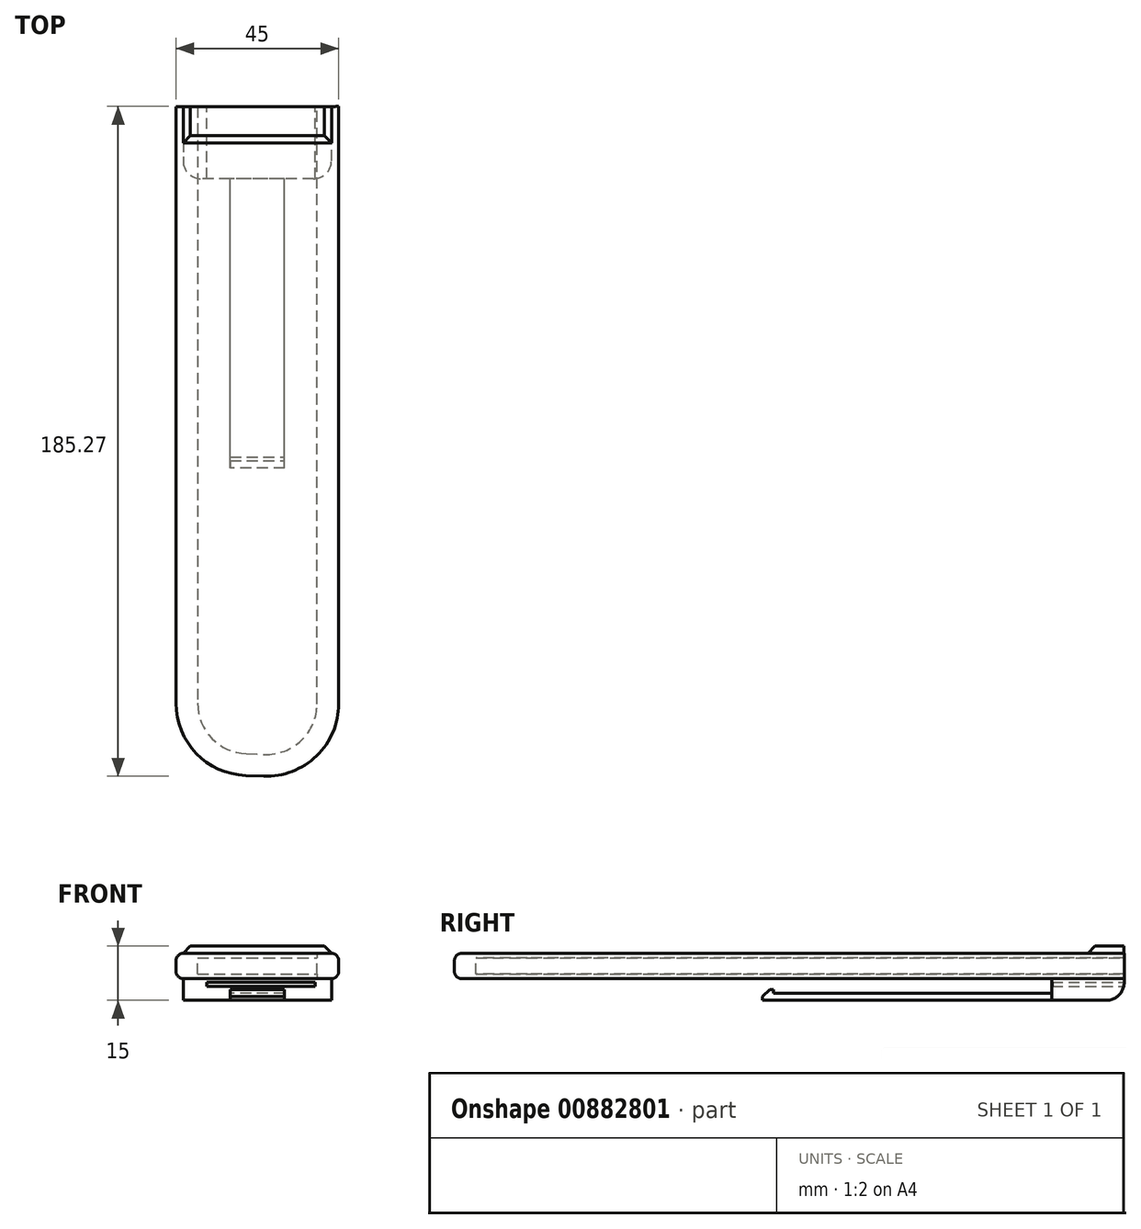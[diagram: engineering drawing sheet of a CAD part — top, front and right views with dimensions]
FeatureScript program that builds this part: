
annotation { "Feature Type Name" : "Feature", "Feature Type Description" : "" }
export const myFeature = defineFeature(function(context is Context, id is Id, definition is map)
    precondition{}
    {
        {
            var Q0;
            Q0=qCreatedBy(makeId("Top.planeOp"),FACE);
            var sketch = newSketch(context, id + "F0", { "sketchPlane" : qUnion([Q0])});
            skLineSegment(sketch, "E0", {"start": v(0, 61.3) * mm, "end": v(0, -148) * mm, "construction": true});
            skLineSegment(sketch, "E1", {"start": v(-16.5, 42.45) * mm, "end": v(16.5, 42.45) * mm});
            skLineSegment(sketch, "E2", {"start": v(-16.5, 42.45) * mm, "end": v(-16.5, -122.55) * mm});
            skLineSegment(sketch, "E3", {"start": v(-3, -136.54) * mm, "end": v(2, -136.72) * mm});
            skLineSegment(sketch, "E4", {"start": v(16.5, -122.73) * mm, "end": v(16.5, 42.45) * mm});
            skPoint(sketch, "E5.visualSharp", {"position": v(-16.5, -136.05) * mm});
            skArc(sketch, "E5.filletArc", {"start": v(-16.5, -122.55) * mm, "mid": v(-12.58, -132.27) * mm, "end": v(-3, -136.54) * mm});
            skPoint(sketch, "E6.visualSharp", {"position": v(16.5, -137.25) * mm});
            skArc(sketch, "E6.filletArc", {"start": v(2, -136.72) * mm, "mid": v(12.22, -132.8) * mm, "end": v(16.5, -122.73) * mm});
            skLineSegment(sketch, "E7.0", {"start": v(22.5, -122.73) * mm, "end": v(22.5, 42.54) * mm});
            skLineSegment(sketch, "E7.1", {"start": v(-22.5, 42.45) * mm, "end": v(-22.5, -122.55) * mm});
            skArc(sketch, "E7.2", {"start": v(-22.5, -122.55) * mm, "mid": v(-16.9, -136.43) * mm, "end": v(-3.23, -142.54) * mm});
            skLineSegment(sketch, "E7.3", {"start": v(-3.23, -142.54) * mm, "end": v(1.77, -142.72) * mm});
            skArc(sketch, "E7.4", {"start": v(1.77, -142.72) * mm, "mid": v(16.38, -137.13) * mm, "end": v(22.5, -122.73) * mm});
            skLineSegment(sketch, "E8", {"start": v(-16.5, 42.45) * mm, "end": v(-22.5, 42.45) * mm});
            skLineSegment(sketch, "E9", {"start": v(16.5, 42.45) * mm, "end": v(22.5, 42.54) * mm});
            skSolve(sketch);
        }
        {
            var Q0;
            Q0=makeQuery(id+"F0.imprint","IMPRINT",FACE,{"disambiguationData":[TD([[makeQuery(id+"F0.imprint","IMPRINT",EDGE,{"derivedFrom":sQuery(id+"F0.wireOp",EDGE,"E2")}),-1.0]])]});
            var Q1;
            Q1=makeQuery(id+"F0.imprint","IMPRINT",FACE,{"disambiguationData":[TD([[makeQuery(id+"F0.imprint","IMPRINT",EDGE,{"derivedFrom":sQuery(id+"F0.wireOp",EDGE,"E1")}),-1.0]])]});
            extrude(context, id + "F1", {"entities" : qUnion([Q0, Q1]), "endBound" : BoundingType.SYMMETRIC, "depth" : 7 * mm, "offsetDistance" : 25 * mm});
        }
        {
            var Q0;
            Q0=makeQuery(id+"F0.imprint","IMPRINT",FACE,{"disambiguationData":[TD([[makeQuery(id+"F0.imprint","IMPRINT",EDGE,{"derivedFrom":sQuery(id+"F0.wireOp",EDGE,"E1")}),-1.0]])]});
            extrude(context, id + "F2", {"entities" : qUnion([Q0]), "operationType" : NewBodyOperationType.REMOVE, "endBound" : BoundingType.SYMMETRIC, "oppositeDirection" : true, "depth" : 4.5 * mm, "offsetDistance" : 25 * mm});
        }
        {
            var Q0;
            Q0=makeQuery(id+"F1.opExtrude","CAP_EDGE",EDGE,{"disambiguationData":[OSD([sQuery(id+"F0.wireOp",EDGE,"E7.0")])],"isStart":false});
            var Q1;
            Q1=makeQuery(id+"F1.opExtrude","CAP_EDGE",EDGE,{"disambiguationData":[OSD([sQuery(id+"F0.wireOp",EDGE,"E7.0")])],"isStart":true});
            fillet(context, id + "F3", {"entities" : qUnion([Q0, Q1]), "radius" : 2 * mm, "tangentPropagation" : true, "allowEdgeOverflow" : false});
        }
        {
            var Q0;
            Q0=makeQuery(id+"F1.opExtrude","CAP_FACE",FACE,{"disambiguationData":[OSD([sQuery(id+"F0.wireOp",EDGE,"E1"),sQuery(id+"F0.wireOp",EDGE,"E7.0"),sQuery(id+"F0.wireOp",EDGE,"E7.1"),sQuery(id+"F0.wireOp",EDGE,"E7.2"),sQuery(id+"F0.wireOp",EDGE,"E7.3"),sQuery(id+"F0.wireOp",EDGE,"E7.4"),sQuery(id+"F0.wireOp",EDGE,"E8"),sQuery(id+"F0.wireOp",EDGE,"E9")])],"isStart":false});
            var sketch = newSketch(context, id + "F4", { "sketchPlane" : qUnion([Q0])});
            skLineSegment(sketch, "E10.bottom", {"start": v(-20.5, 42.45) * mm, "end": v(20.5, 42.45) * mm});
            skLineSegment(sketch, "E10.top", {"start": v(-20.5, 32.45) * mm, "end": v(20.5, 32.45) * mm});
            skLineSegment(sketch, "E10.left", {"start": v(-20.5, 42.45) * mm, "end": v(-20.5, 32.45) * mm});
            skLineSegment(sketch, "E10.right", {"start": v(20.5, 42.45) * mm, "end": v(20.5, 32.45) * mm});
            skSolve(sketch);
        }
        {
            var Q0;
            Q0 = qSketchRegion(id + "F4", true);
            extrude(context, id + "F5", {"entities" : qUnion([Q0]), "operationType" : NewBodyOperationType.ADD, "depth" : 2 * mm, "offsetDistance" : 25 * mm});
        }
        {
            var Q0;
            Q0=makeQuery(id+"F5.opExtrude","CAP_EDGE",EDGE,{"disambiguationData":[OSD([sQuery(id+"F4.wireOp",EDGE,"E10.right")])],"isStart":false});
            var Q1;
            Q1=makeQuery(id+"F5.opExtrude","CAP_EDGE",EDGE,{"disambiguationData":[OSD([sQuery(id+"F4.wireOp",EDGE,"E10.top")])],"isStart":false});
            var Q2;
            Q2=makeQuery(id+"F5.opExtrude","CAP_EDGE",EDGE,{"disambiguationData":[OSD([sQuery(id+"F4.wireOp",EDGE,"E10.left")])],"isStart":false});
            chamfer(context, id + "F6", {"entities" : qUnion([Q0, Q1, Q2]), "width" : 2 * mm, "tangentPropagation" : true});
        }
        {
            var Q0;
            Q0=makeQuery(id+"F1.opExtrude","CAP_FACE",FACE,{"disambiguationData":[OSD([sQuery(id+"F0.wireOp",EDGE,"E1"),sQuery(id+"F0.wireOp",EDGE,"E7.0"),sQuery(id+"F0.wireOp",EDGE,"E7.1"),sQuery(id+"F0.wireOp",EDGE,"E7.2"),sQuery(id+"F0.wireOp",EDGE,"E7.3"),sQuery(id+"F0.wireOp",EDGE,"E7.4"),sQuery(id+"F0.wireOp",EDGE,"E8"),sQuery(id+"F0.wireOp",EDGE,"E9")])],"isStart":true});
            var sketch = newSketch(context, id + "F7", { "sketchPlane" : qUnion([Q0])});
            skLineSegment(sketch, "E11.bottom", {"start": v(20.5, -42.5) * mm, "end": v(-20.5, -42.5) * mm});
            skLineSegment(sketch, "E11.top", {"start": v(20.5, -22.5) * mm, "end": v(-20.5, -22.5) * mm});
            skLineSegment(sketch, "E11.left", {"start": v(20.5, -42.5) * mm, "end": v(20.5, -22.5) * mm});
            skLineSegment(sketch, "E11.right", {"start": v(-20.5, -42.5) * mm, "end": v(-20.5, -22.5) * mm});
            skSolve(sketch);
        }
        {
            var Q0;
            Q0 = qSketchRegion(id + "F7", true);
            extrude(context, id + "F8", {"entities" : qUnion([Q0]), "operationType" : NewBodyOperationType.ADD, "depth" : 6 * mm, "offsetDistance" : 25 * mm});
        }
        {
            var Q0;
            Q0=makeQuery(id+"F8.opExtrude","SWEPT_EDGE",EDGE,{"disambiguationData":[OSD([sQuery(id+"F0.wireOp",EDGE,"E1"),sQuery(id+"F0.wireOp",EDGE,"E7.0"),sQuery(id+"F0.wireOp",EDGE,"E7.1"),sQuery(id+"F0.wireOp",EDGE,"E7.2"),sQuery(id+"F0.wireOp",EDGE,"E7.3"),sQuery(id+"F0.wireOp",EDGE,"E7.4"),sQuery(id+"F0.wireOp",EDGE,"E8"),sQuery(id+"F0.wireOp",EDGE,"E9"),sQuery(id+"F7.wireOp",EDGE,"E11.top"),sQuery(id+"F7.wireOp",EDGE,"E11.right")])]});
            var Q1;
            Q1=makeQuery(id+"F8.opExtrude","SWEPT_EDGE",EDGE,{"disambiguationData":[OSD([sQuery(id+"F0.wireOp",EDGE,"E1"),sQuery(id+"F0.wireOp",EDGE,"E7.0"),sQuery(id+"F0.wireOp",EDGE,"E7.1"),sQuery(id+"F0.wireOp",EDGE,"E7.2"),sQuery(id+"F0.wireOp",EDGE,"E7.3"),sQuery(id+"F0.wireOp",EDGE,"E7.4"),sQuery(id+"F0.wireOp",EDGE,"E8"),sQuery(id+"F0.wireOp",EDGE,"E9"),sQuery(id+"F7.wireOp",EDGE,"E11.top"),sQuery(id+"F7.wireOp",EDGE,"E11.left")])]});
            var Q2;
            Q2=makeQuery(id+"F8.opExtrude","CAP_EDGE",EDGE,{"disambiguationData":[OSD([sQuery(id+"F7.wireOp",EDGE,"E11.bottom")])],"isStart":false});
            fillet(context, id + "F9", {"entities" : qUnion([Q0, Q1, Q2]), "radius" : 5 * mm, "tangentPropagation" : true, "allowEdgeOverflow" : false});
        }
        {
            var Q0;
            Q0=makeQuery(id+"F8.opExtrude","SWEPT_FACE",FACE,{"disambiguationData":[OSD([sQuery(id+"F7.wireOp",EDGE,"E11.top")])]});
            var sketch = newSketch(context, id + "F10", { "sketchPlane" : qUnion([Q0])});
            skLineSegment(sketch, "E12.bottom", {"start": v(7.5, -9.5) * mm, "end": v(-7.5, -9.5) * mm});
            skLineSegment(sketch, "E12.top", {"start": v(7.5, -7.5) * mm, "end": v(-7.5, -7.5) * mm});
            skLineSegment(sketch, "E12.left", {"start": v(7.5, -9.5) * mm, "end": v(7.5, -7.5) * mm});
            skLineSegment(sketch, "E12.right", {"start": v(-7.5, -9.5) * mm, "end": v(-7.5, -7.5) * mm});
            skSolve(sketch);
        }
        {
            var Q0;
            Q0 = qSketchRegion(id + "F10", true);
            extrude(context, id + "F11", {"entities" : qUnion([Q0]), "operationType" : NewBodyOperationType.ADD, "depth" : 80 * mm, "offsetDistance" : 25 * mm});
        }
        {
            var Q0;
            Q0=makeQuery(id+"F11.opExtrude","SWEPT_FACE",FACE,{"disambiguationData":[OSD([sQuery(id+"F10.wireOp",EDGE,"E12.top")])]});
            var sketch = newSketch(context, id + "F12", { "sketchPlane" : qUnion([Q0])});
            skLineSegment(sketch, "E13.bottom", {"start": v(-7.5, -57.5) * mm, "end": v(7.5, -57.5) * mm});
            skLineSegment(sketch, "E13.top", {"start": v(-7.5, -54.5) * mm, "end": v(7.5, -54.5) * mm});
            skLineSegment(sketch, "E13.left", {"start": v(-7.5, -57.5) * mm, "end": v(-7.5, -54.5) * mm});
            skLineSegment(sketch, "E13.right", {"start": v(7.5, -57.5) * mm, "end": v(7.5, -54.5) * mm});
            skSolve(sketch);
        }
        {
            var Q0;
            Q0 = qSketchRegion(id + "F12", true);
            extrude(context, id + "F13", {"entities" : qUnion([Q0]), "operationType" : NewBodyOperationType.ADD, "depth" : 1 * mm, "offsetDistance" : 25 * mm});
        }
        {
            var Q0;
            Q0=makeQuery(id+"F13.opExtrude","CAP_EDGE",EDGE,{"disambiguationData":[OSD([sQuery(id+"F12.wireOp",EDGE,"E13.bottom")])],"isStart":false});
            chamfer(context, id + "F14", {"entities" : qUnion([Q0]), "width" : 2 * mm, "tangentPropagation" : true});
        }
        {
            var Q0;
            Q0=makeQuery(id+"F8.opExtrude","SWEPT_FACE",FACE,{"disambiguationData":[OSD([sQuery(id+"F7.wireOp",EDGE,"E11.bottom")])]});
            var sketch = newSketch(context, id + "F15", { "sketchPlane" : qUnion([Q0])});
            skLineSegment(sketch, "E14.bottom", {"start": v(14, -4.5) * mm, "end": v(-16, -4.5) * mm});
            skLineSegment(sketch, "E14.top", {"start": v(14, -5.7) * mm, "end": v(-16, -5.7) * mm});
            skLineSegment(sketch, "E14.left", {"start": v(14, -4.5) * mm, "end": v(14, -5.7) * mm});
            skLineSegment(sketch, "E14.right", {"start": v(-16, -4.5) * mm, "end": v(-16, -5.7) * mm});
            skSolve(sketch);
        }
        {
            var Q0;
            Q0 = qSketchRegion(id + "F15", true);
            extrude(context, id + "F16", {"entities" : qUnion([Q0]), "operationType" : NewBodyOperationType.REMOVE, "oppositeDirection" : true, "depth" : 25 * mm, "offsetDistance" : 25 * mm});
        }
    });
